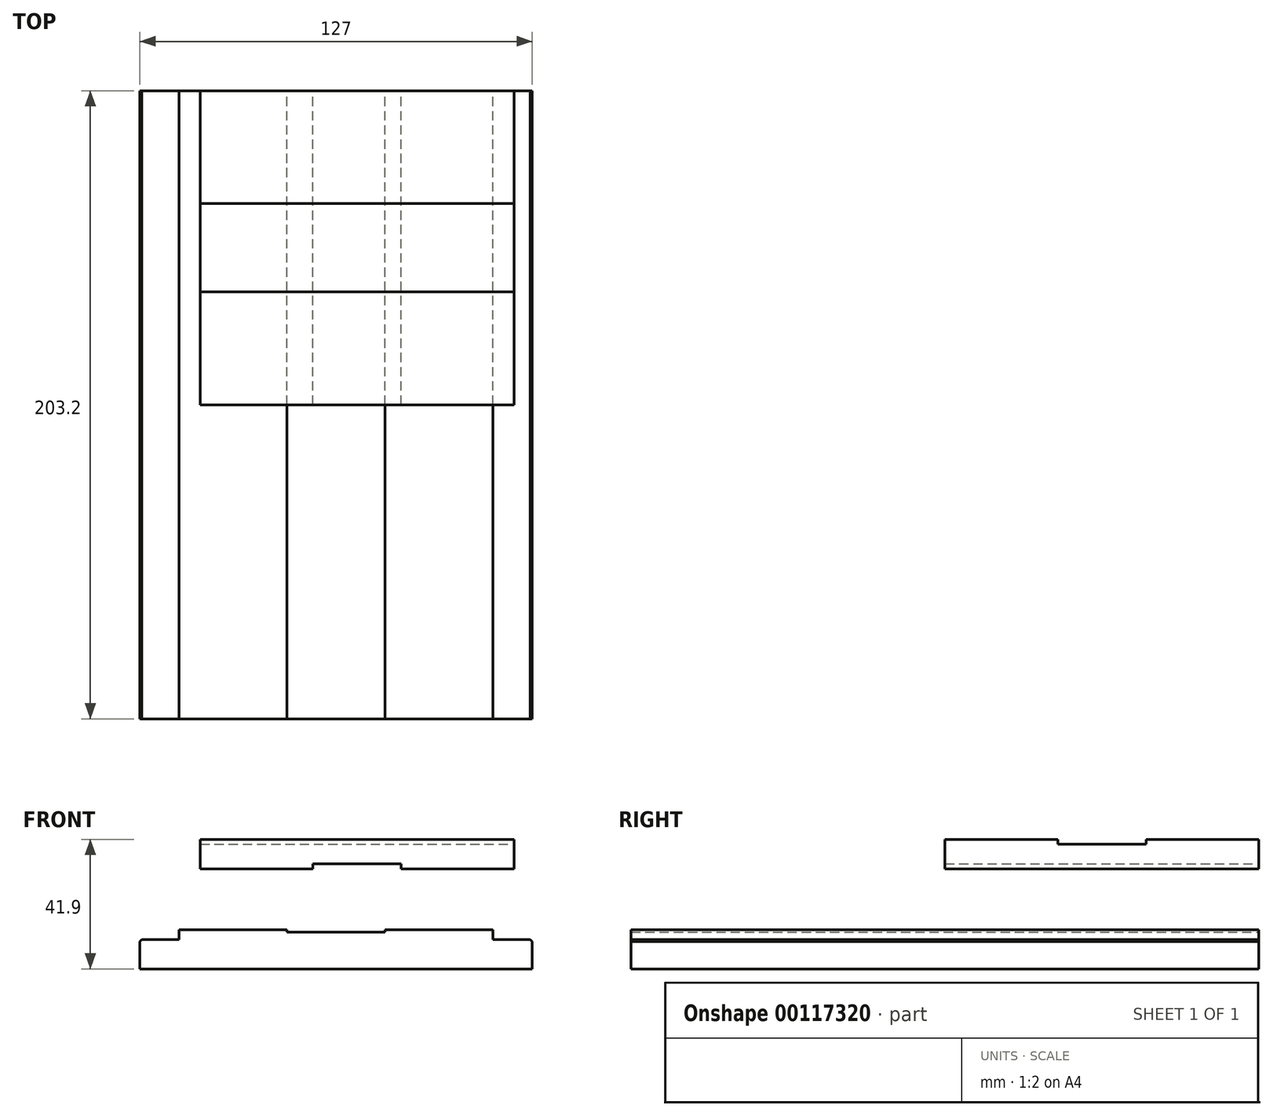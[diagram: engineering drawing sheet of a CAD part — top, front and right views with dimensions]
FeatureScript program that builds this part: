
annotation { "Feature Type Name" : "Feature", "Feature Type Description" : "" }
export const myFeature = defineFeature(function(context is Context, id is Id, definition is map)
    precondition{}
    {
        {
            var Q0;
            Q0=qCreatedBy(makeId("Front.planeOp"),FACE);
            var sketch = newSketch(context, id + "F0", { "sketchPlane" : qUnion([Q0])});
            skLineSegment(sketch, "E0.bottom", {"start": v(63.5, -6.35) * mm, "end": v(-63.5, -6.35) * mm});
            skLineSegment(sketch, "E0.top", {"start": v(50.8, 6.35) * mm, "end": v(15.87, 6.35) * mm});
            skLineSegment(sketch, "E0.left", {"start": v(63.5, -6.35) * mm, "end": v(63.5, 6.35) * mm});
            skLineSegment(sketch, "E0.right", {"start": v(-63.5, -6.35) * mm, "end": v(-63.5, 3.17) * mm});
            skPoint(sketch, "E0.middle", {"position": v(0, 0) * mm});
            skLineSegment(sketch, "E1", {"start": v(-15.88, 6.35) * mm, "end": v(-15.88, 5.56) * mm});
            skLineSegment(sketch, "E2", {"start": v(15.87, 6.35) * mm, "end": v(15.87, 5.56) * mm});
            skPoint(sketch, "E3.orphan", {"position": v(-63.5, 6.35) * mm});
            skLineSegment(sketch, "E4.trimOffspring", {"start": v(-15.88, 6.35) * mm, "end": v(-50.8, 6.35) * mm});
            skPoint(sketch, "E5.orphan", {"position": v(63.5, 6.35) * mm});
            skLineSegment(sketch, "E6.trimOffspring", {"start": v(-15.88, 5.56) * mm, "end": v(15.87, 5.56) * mm});
            skLineSegment(sketch, "E7", {"start": v(-63.5, 3.17) * mm, "end": v(-50.8, 3.17) * mm});
            skLineSegment(sketch, "E8", {"start": v(-50.8, 6.35) * mm, "end": v(-50.8, 3.17) * mm});
            skLineSegment(sketch, "E9", {"start": v(50.8, 6.35) * mm, "end": v(50.8, 3.17) * mm});
            skLineSegment(sketch, "E10.trimOffspring", {"start": v(50.8, 3.17) * mm, "end": v(63.5, 3.17) * mm});
            skSolve(sketch);
        }
        {
            var Q0;
            Q0=makeQuery(id+"F0.imprint","IMPRINT",FACE,{"disambiguationData":[TD([[makeQuery(id+"F0.imprint","IMPRINT",EDGE,{"derivedFrom":sQuery(id+"F0.wireOp",EDGE,"E0.bottom")}),-1.0]])]});
            extrude(context, id + "F1", {"entities" : qUnion([Q0]), "depth" : 203.2 * mm});
        }
        {
            var Q0;
            Q0=qCreatedBy(makeId("Front.planeOp"),FACE);
            var sketch = newSketch(context, id + "F2", { "sketchPlane" : qUnion([Q0])});
            skLineSegment(sketch, "E11.bottom", {"start": v(-43.98, 35.55) * mm, "end": v(57.62, 35.55) * mm});
            skLineSegment(sketch, "E11.top", {"start": v(-43.98, 26.02) * mm, "end": v(-7.47, 26.02) * mm});
            skLineSegment(sketch, "E11.left", {"start": v(-43.98, 35.55) * mm, "end": v(-43.98, 26.02) * mm});
            skLineSegment(sketch, "E11.right", {"start": v(57.62, 35.55) * mm, "end": v(57.62, 26.02) * mm});
            skLineSegment(sketch, "E12", {"start": v(-7.47, 27.6) * mm, "end": v(21.1, 27.6) * mm});
            skLineSegment(sketch, "E13", {"start": v(-7.47, 27.6) * mm, "end": v(-7.47, 26.02) * mm});
            skLineSegment(sketch, "E14", {"start": v(21.1, 27.6) * mm, "end": v(21.1, 26.02) * mm});
            skLineSegment(sketch, "E15.trimOffspring", {"start": v(21.1, 26.02) * mm, "end": v(57.62, 26.02) * mm});
            skSolve(sketch);
        }
        {
            var Q0;
            Q0=makeQuery(id+"F2.imprint","IMPRINT",FACE,{"disambiguationData":[TD([[makeQuery(id+"F2.imprint","IMPRINT",EDGE,{"derivedFrom":sQuery(id+"F2.wireOp",EDGE,"E11.bottom")}),-1.0]])]});
            extrude(context, id + "F3", {"entities" : qUnion([Q0]), "depth" : 101.6 * mm});
        }
        {
            var Q0;
            Q0=makeQuery(id+"F3.opExtrude","SWEPT_FACE",FACE,{"disambiguationData":[OSD([sQuery(id+"F2.wireOp",EDGE,"E11.right")])]});
            var sketch = newSketch(context, id + "F4", { "sketchPlane" : qUnion([Q0])});
            skLineSegment(sketch, "E16.0.0", {"start": v(0, 26.02) * mm, "end": v(0, 35.55) * mm, "construction": true});
            skLineSegment(sketch, "E16.0.1", {"start": v(0, 35.55) * mm, "end": v(-101.6, 35.55) * mm, "construction": true});
            skLineSegment(sketch, "E16.0.2", {"start": v(-101.6, 35.55) * mm, "end": v(-101.6, 26.02) * mm, "construction": true});
            skLineSegment(sketch, "E16.0.3", {"start": v(-101.6, 26.02) * mm, "end": v(0, 26.02) * mm, "construction": true});
            skLineSegment(sketch, "E17", {"start": v(-65.09, 33.97) * mm, "end": v(-36.51, 33.97) * mm});
            skLineSegment(sketch, "E18", {"start": v(-50.8, 35.55) * mm, "end": v(-50.8, 26.02) * mm, "construction": true});
            skLineSegment(sketch, "E19", {"start": v(-65.09, 35.55) * mm, "end": v(-65.09, 33.97) * mm});
            skLineSegment(sketch, "E20", {"start": v(-36.51, 35.55) * mm, "end": v(-36.51, 33.97) * mm});
            skLineSegment(sketch, "E21", {"start": v(-65.09, 35.55) * mm, "end": v(-36.51, 35.55) * mm});
            skSolve(sketch);
        }
        {
            var Q0;
            Q0=makeQuery(id+"F4.imprint","IMPRINT",FACE,{"disambiguationData":[TD([[makeQuery(id+"F4.imprint","IMPRINT",EDGE,{"derivedFrom":sQuery(id+"F4.wireOp",EDGE,"E17")}),1.0]])]});
            extrude(context, id + "F5", {"entities" : qUnion([Q0]), "operationType" : NewBodyOperationType.REMOVE, "endBound" : BoundingType.THROUGH_ALL, "oppositeDirection" : true, "depth" : 25.4 * mm});
        }
        {
            var Q0;
            Q0=makeQuery(id+"F1.opExtrude","SWEPT_EDGE",EDGE,{"disambiguationData":[OSD([sQuery(id+"F0.wireOp",EDGE,"E0.right"),sQuery(id+"F0.wireOp",EDGE,"E7")])]});
            var Q1;
            Q1=makeQuery(id+"F1.opExtrude","SWEPT_EDGE",EDGE,{"disambiguationData":[OSD([sQuery(id+"F0.wireOp",EDGE,"E0.left"),sQuery(id+"F0.wireOp",EDGE,"E10.trimOffspring")])]});
            chamfer(context, id + "F6", {"entities" : qUnion([Q0, Q1]), "width" : 0.64 * mm, "tangentPropagation" : true});
        }
    });
